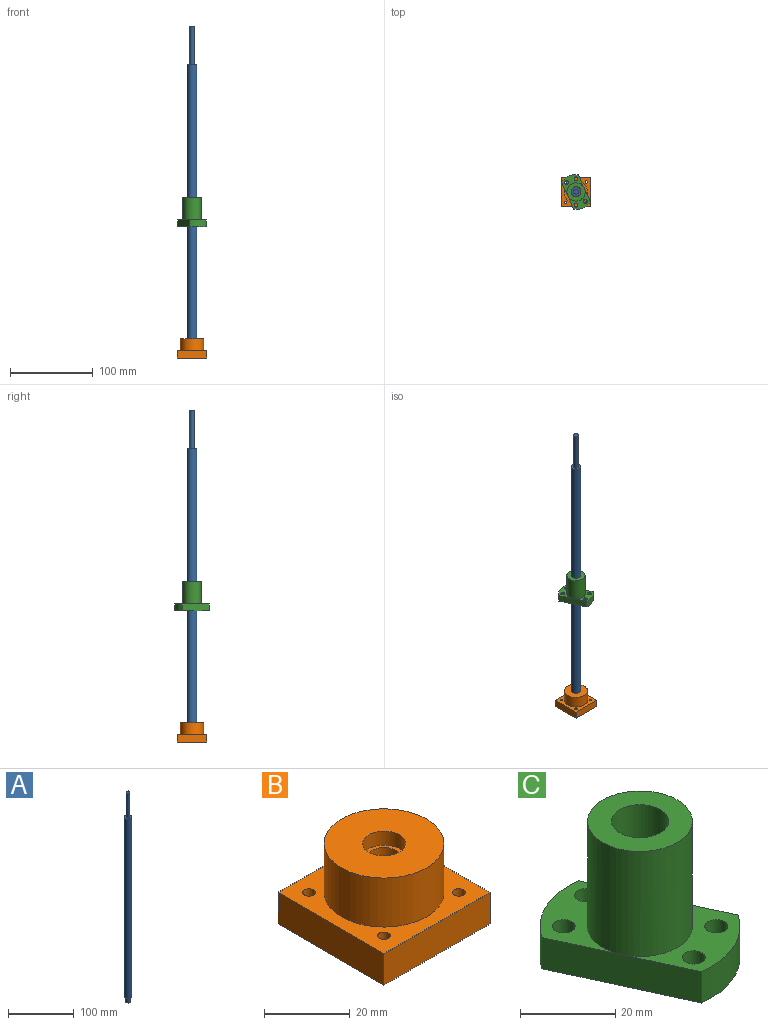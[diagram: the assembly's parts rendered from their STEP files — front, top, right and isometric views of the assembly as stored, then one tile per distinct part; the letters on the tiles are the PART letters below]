
ASSEMBLY  parts=3 mates=3
PART A: 7 faces, bbox 12x12x391.5 mm
  f0: cylinder r=4mm len=10mm, axis (0,0,-1), area 251.3mm2, adj f1,f4
  f1: plane 8x8mm, normal (0,0,-1), area 50.3mm2, adj f0
  f2: cylinder r=6mm len=335mm, axis (0,0,-1), area 12629.2mm2, adj f3,f4
  f3: plane 12x12mm, normal (0,0,1), area 84.8mm2, adj f2,f5
  f4: plane 12x12mm, normal (0,0,-1), area 62.8mm2, adj f0,f2
  f5: cylinder r=3mm len=46.5mm, axis (0,0,-1), area 876.5mm2, adj f3,f6
  f6: plane 6x6mm, normal (0,0,1), area 28.3mm2, adj f5
PART B: 15 faces, bbox 35x35x23 mm
  f0: plane 35x9mm, normal (0,-1,0), area 315mm2, adj f1,f3,f4,f5
  f1: plane 35x9mm, normal (1,0,0), area 315mm2, adj f0,f2,f4,f5
  f2: plane 35x9mm, normal (0,1,0), area 315mm2, adj f1,f3,f4,f5
  f3: plane 35x9mm, normal (-1,0,0), area 315mm2, adj f0,f2,f4,f5
  f4: plane 35x35mm, normal (0,0,1), area 581mm2, adj f0,f1,f2,f3,f6,f11,f12,f13
  f5: plane 35x35mm, normal (0,0,-1), area 1146.5mm2, adj f0,f1,f2,f3,f10,f11,f12,f13
  f6: cylinder r=14mm len=28mm, axis (0,0,-1), area 1231.5mm2, adj f4,f7
  f7: plane 28x28mm, normal (0,0,1), area 537.2mm2, adj f6,f8
  f8: cylinder r=5mm len=10mm, axis (0,0,1), area 125.7mm2, adj f7,f9
  f9: plane 10x10mm, normal (0,0,1), area 28.3mm2, adj f8,f10
  f10: cylinder r=4mm len=19mm, axis (0,0,1), area 477.5mm2, adj f5,f9
  f11: cylinder r=1.5mm len=9mm, axis (0,0,1), area 84.8mm2, adj f4,f5
  f12: cylinder r=1.5mm len=9mm, axis (0,0,1), area 84.8mm2, adj f4,f5
  f13: cylinder r=1.5mm len=9mm, axis (0,0,1), area 84.8mm2, adj f4,f5
  f14: cylinder r=1.5mm len=9mm, axis (0,0,1), area 84.8mm2, adj f4,f5
PART C: 14 faces, bbox 34.9x42x35 mm
  f0: cylinder r=21mm len=20.01mm, axis (0,0,-1), area 185.2mm2, adj f1,f3,f9,f10
  f1: plane 27.45x25.58mm, normal (0,0,1), area 213.6mm2, adj f0,f5,f9,f10,f12,f13
  f2: plane 27.45x25.58mm, normal (0,0,1), area 213.6mm2, adj f4,f5,f8,f9,f10,f11
  f3: plane 42x34.89mm, normal (0,0,-1), area 694.3mm2, adj f0,f4,f7,f8,f9,f10,f11,f12
  f4: cylinder r=21mm len=20.01mm, axis (0,0,-1), area 185.2mm2, adj f2,f3,f9,f10
  f5: cylinder r=11mm len=27mm, axis (0,0,-1), area 1866.1mm2, adj f1,f2,f6
  f6: plane 22x22mm, normal (0,0,1), area 267mm2, adj f5,f7
  f7: cylinder r=6mm len=35mm, axis (0,0,1), area 1319.5mm2, adj f3,f6
  f8: cylinder r=2.4mm len=8mm, axis (0,0,1), area 120.6mm2, adj f2,f3
  f9: plane 32.54x14.88mm, normal (0.91,0.42,0), area 286.2mm2, adj f0,f1,f2,f3,f4
  f10: plane 32.54x14.88mm, normal (-0.91,-0.42,0), area 286.2mm2, adj f0,f1,f2,f3,f4
  f11: cylinder r=2.4mm len=8mm, axis (0,0,1), area 120.6mm2, adj f2,f3
  f12: cylinder r=2.4mm len=8mm, axis (0,0,1), area 120.6mm2, adj f1,f3
  f13: cylinder r=2.4mm len=8mm, axis (0,0,1), area 120.6mm2, adj f1,f3
PLACE A t=(13.3,-31.48,-148.1)mm
PLACE B t=(13.3,-31.48,-157.1)mm
PLACE C t=(13.3,-31.48,1.38)mm
MATE planar B.f8 <-> A.f2  axis (0,0,1) through (13.3,-31.48,-138.1)mm
MATE cylindrical A.f2 <-> C.f7  axis (0,0,-1) through (13.3,-31.48,29.4)mm
MATE cylindrical A.f2 <-> B.f8  axis (0,0,-1) through (13.3,-31.48,29.4)mm
